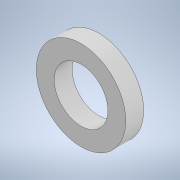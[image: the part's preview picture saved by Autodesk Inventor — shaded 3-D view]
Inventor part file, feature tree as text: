
AUTODESK INVENTOR PART (.ipt)
format: ipt  version: 2021 (Build 250183000, 183)  size: 100,352 bytes
history: native  units: in
note: dims shown in document units (in); Inventor stores cm internally (conversion verified against a paired STEP export)
features: extrude x1, sketch x1
ambient origin geometry x8: Origin, YZ Plane, XZ Plane, XY Plane, X Axis, Y Axis, Z Axis, Center Point
bodies: Solid1 (feature_tree)
feature tree (2):
  extrude  "Extrusion1"  Depth=0.0157in
  sketch  "Sketch1"  dims[d0=0.0472in d1=0.0787in d2=0.0157in d3=0.0in]
